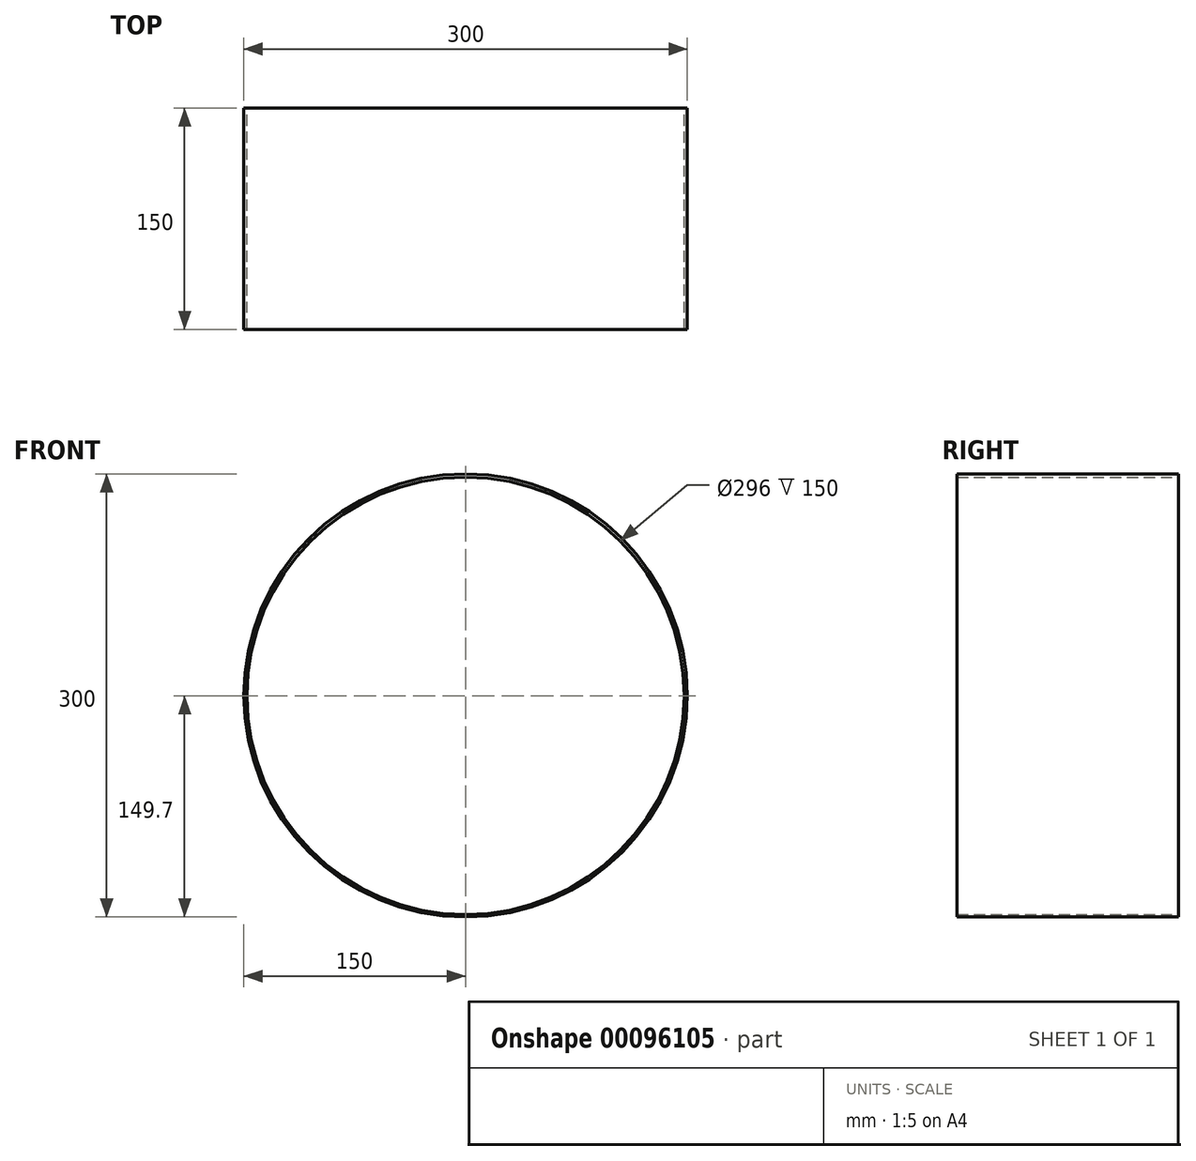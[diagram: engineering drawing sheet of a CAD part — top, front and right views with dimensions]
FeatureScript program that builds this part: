
annotation { "Feature Type Name" : "Feature", "Feature Type Description" : "" }
export const myFeature = defineFeature(function(context is Context, id is Id, definition is map)
    precondition{}
    {
        {
            var Q0;
            Q0=qCreatedBy(makeId("Front.planeOp"),FACE);
            var sketch = newSketch(context, id + "F0", { "sketchPlane" : qUnion([Q0])});
            skCircle(sketch, "E0", {"center": v(0, 0) * mm, "radius": 150 * mm});
            skCircle(sketch, "E1", {"center": v(0, -0.3) * mm, "radius": 148 * mm});
            skSolve(sketch);
        }
        {
            var Q0;
            Q0 = qSketchRegion(id + "F0", true);
            var Q1;
            Q1=makeQuery(id+"F0.imprint","IMPRINT",FACE,{"disambiguationData":[TD([[makeQuery(id+"F0.imprint","IMPRINT",EDGE,{"derivedFrom":sQuery(id+"F0.wireOp",EDGE,"E0")}),1.0]])]});
            extrude(context, id + "F1", {"entities" : qUnion([Q0, Q1]), "depth" : 150 * mm});
        }
    });
